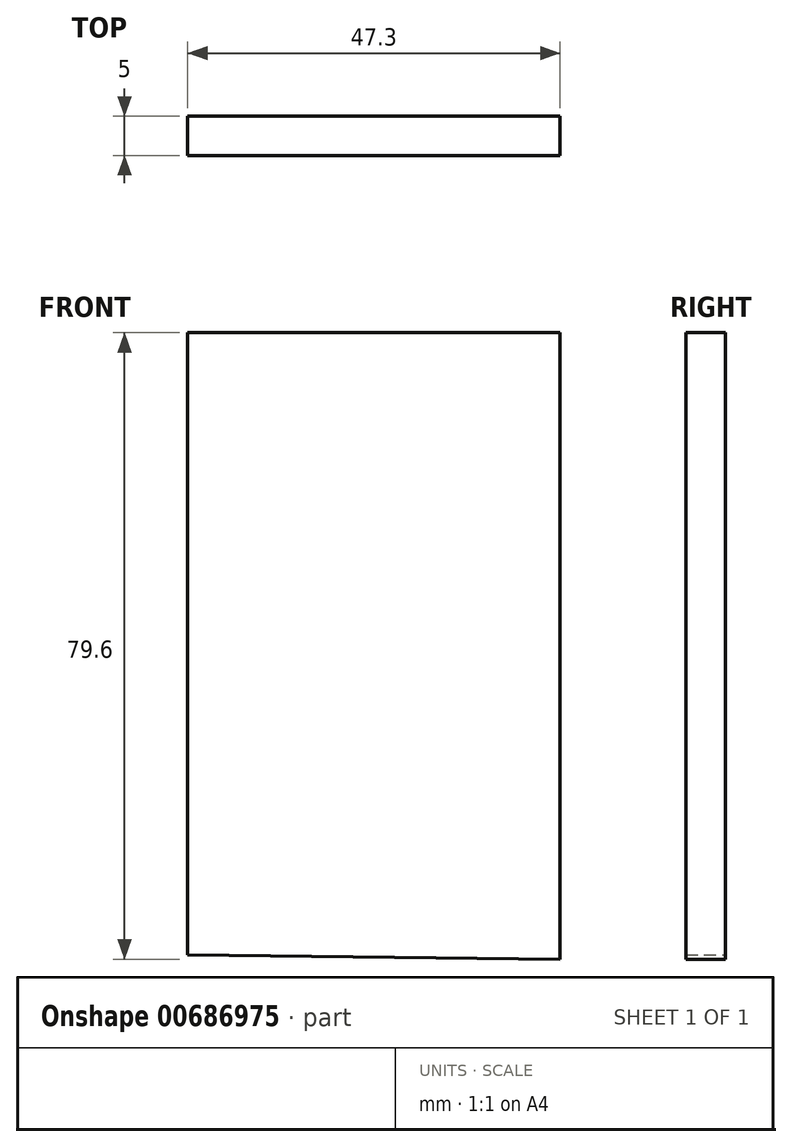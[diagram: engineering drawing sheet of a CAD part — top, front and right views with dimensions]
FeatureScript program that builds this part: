
annotation { "Feature Type Name" : "Feature", "Feature Type Description" : "" }
export const myFeature = defineFeature(function(context is Context, id is Id, definition is map)
    precondition{}
    {
        {
            var Q0;
            Q0=qCreatedBy(makeId("Front.planeOp"),FACE);
            var sketch = newSketch(context, id + "F0", { "sketchPlane" : qUnion([Q0])});
            skLineSegment(sketch, "E0", {"start": v(-40.08, 28.75) * mm, "end": v(-40.08, -40.93) * mm});
            skLineSegment(sketch, "E1", {"start": v(-40.08, 28.75) * mm, "end": v(-40.08, 38.1) * mm});
            skLineSegment(sketch, "E2", {"start": v(-40.08, 38.1) * mm, "end": v(7.22, 38.1) * mm});
            skLineSegment(sketch, "E3", {"start": v(7.22, 38.1) * mm, "end": v(7.22, -41.5) * mm});
            skLineSegment(sketch, "E4", {"start": v(7.22, -41.5) * mm, "end": v(-40.08, -40.93) * mm});
            skSolve(sketch);
        }
        {
            var Q0;
            Q0=makeQuery(id+"F0.imprint","IMPRINT",FACE,{"disambiguationData":[TD([[makeQuery(id+"F0.imprint","IMPRINT",EDGE,{"derivedFrom":sQuery(id+"F0.wireOp",EDGE,"E0")}),1.0]])]});
            extrude(context, id + "F1", {"entities" : qUnion([Q0]), "depth" : 5 * mm, "offsetDistance" : 25 * mm});
        }
    });
